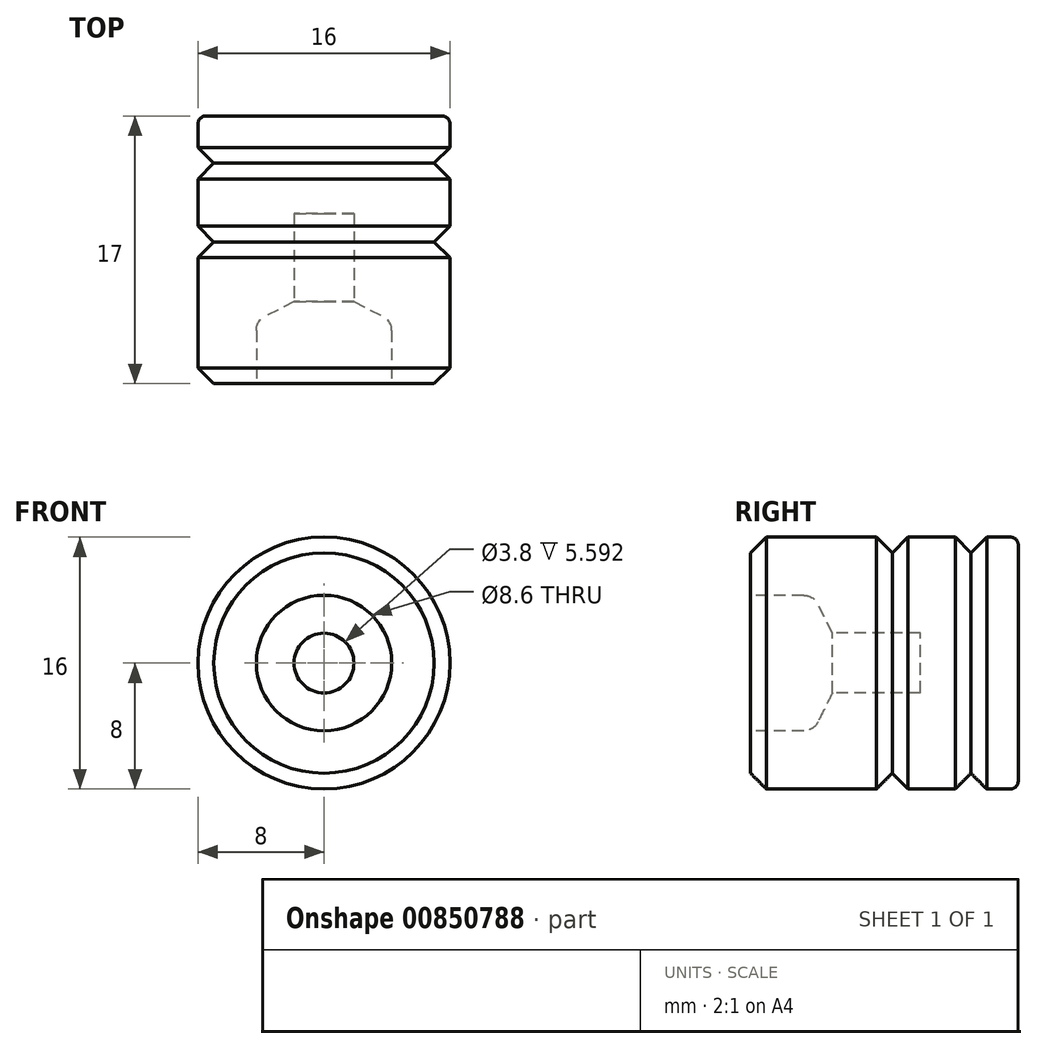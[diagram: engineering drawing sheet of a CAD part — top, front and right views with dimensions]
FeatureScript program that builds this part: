
annotation { "Feature Type Name" : "Feature", "Feature Type Description" : "" }
export const myFeature = defineFeature(function(context is Context, id is Id, definition is map)
    precondition{}
    {
        {
            var Q0;
            Q0=qCreatedBy(makeId("Top.planeOp"),FACE);
            var sketch = newSketch(context, id + "F0", { "sketchPlane" : qUnion([Q0])});
            skLineSegment(sketch, "E0", {"start": v(0, 0) * mm, "end": v(0, 17.06) * mm, "construction": true});
            skLineSegment(sketch, "E1", {"start": v(1.9, 5.2) * mm, "end": v(1.9, 10.8) * mm});
            skLineSegment(sketch, "E2", {"start": v(1.9, 10.8) * mm, "end": v(0, 10.8) * mm});
            skLineSegment(sketch, "E3", {"start": v(0, 10.8) * mm, "end": v(0, 17) * mm});
            skLineSegment(sketch, "E4", {"start": v(0, 17) * mm, "end": v(8, 17) * mm});
            skLineSegment(sketch, "E5", {"start": v(8, 17) * mm, "end": v(8, 15) * mm});
            skLineSegment(sketch, "E6", {"start": v(8, 15) * mm, "end": v(7, 14) * mm});
            skLineSegment(sketch, "E7", {"start": v(7, 14) * mm, "end": v(8, 13) * mm});
            skLineSegment(sketch, "E8", {"start": v(8, 13) * mm, "end": v(8, 10) * mm});
            skLineSegment(sketch, "E9", {"start": v(8, 10) * mm, "end": v(7, 9) * mm});
            skLineSegment(sketch, "E10", {"start": v(7, 9) * mm, "end": v(8, 8) * mm});
            skLineSegment(sketch, "E11", {"start": v(8, 8) * mm, "end": v(8, 0) * mm});
            skLineSegment(sketch, "E12", {"start": v(4.3, 0) * mm, "end": v(8, 0) * mm});
            skLineSegment(sketch, "E13", {"start": v(4.3, 4) * mm, "end": v(4.3, 0) * mm});
            skLineSegment(sketch, "E14", {"start": v(4.3, 4) * mm, "end": v(1.9, 5.2) * mm});
            skPoint(sketch, "E15.orphan", {"position": v(1.9, 0) * mm});
            skSolve(sketch);
        }
        {
            var Q0;
            Q0=qSketchRegion(id+"F0",true);
            var Q1;
            Q1=sQuery(id+"F0.wireOp",EDGE,"E0");
            revolve(context, id + "F1", {"entities" : qUnion([Q0]), "axis" : qUnion([Q1]), "revolveType" : RevolveType.FULL});
        }
        {
            var Q0;
            Q0=makeQuery(id+"F1.opRevolve","SWEPT_EDGE",EDGE,{"disambiguationData":[OSD([sQuery(id+"F0.wireOp",EDGE,"E13"),sQuery(id+"F0.wireOp",EDGE,"E14")])]});
            fillet(context, id + "F2", {"entities" : qUnion([Q0]), "radius" : 1 * mm, "tangentPropagation" : true, "allowEdgeOverflow" : false});
        }
        {
            var Q0;
            Q0=makeQuery(id+"F1.opRevolve","SWEPT_EDGE",EDGE,{"disambiguationData":[OSD([sQuery(id+"F0.wireOp",EDGE,"E4"),sQuery(id+"F0.wireOp",EDGE,"E5")])]});
            fillet(context, id + "F3", {"entities" : qUnion([Q0]), "radius" : 0.5 * mm, "tangentPropagation" : true, "allowEdgeOverflow" : false});
        }
        {
            var Q0;
            Q0=makeQuery(id+"F1.opRevolve","SWEPT_EDGE",EDGE,{"disambiguationData":[OSD([sQuery(id+"F0.wireOp",EDGE,"E11"),sQuery(id+"F0.wireOp",EDGE,"E12")])]});
            chamfer(context, id + "F4", {"entities" : qUnion([Q0]), "width" : 1 * mm, "tangentPropagation" : true});
        }
    });
